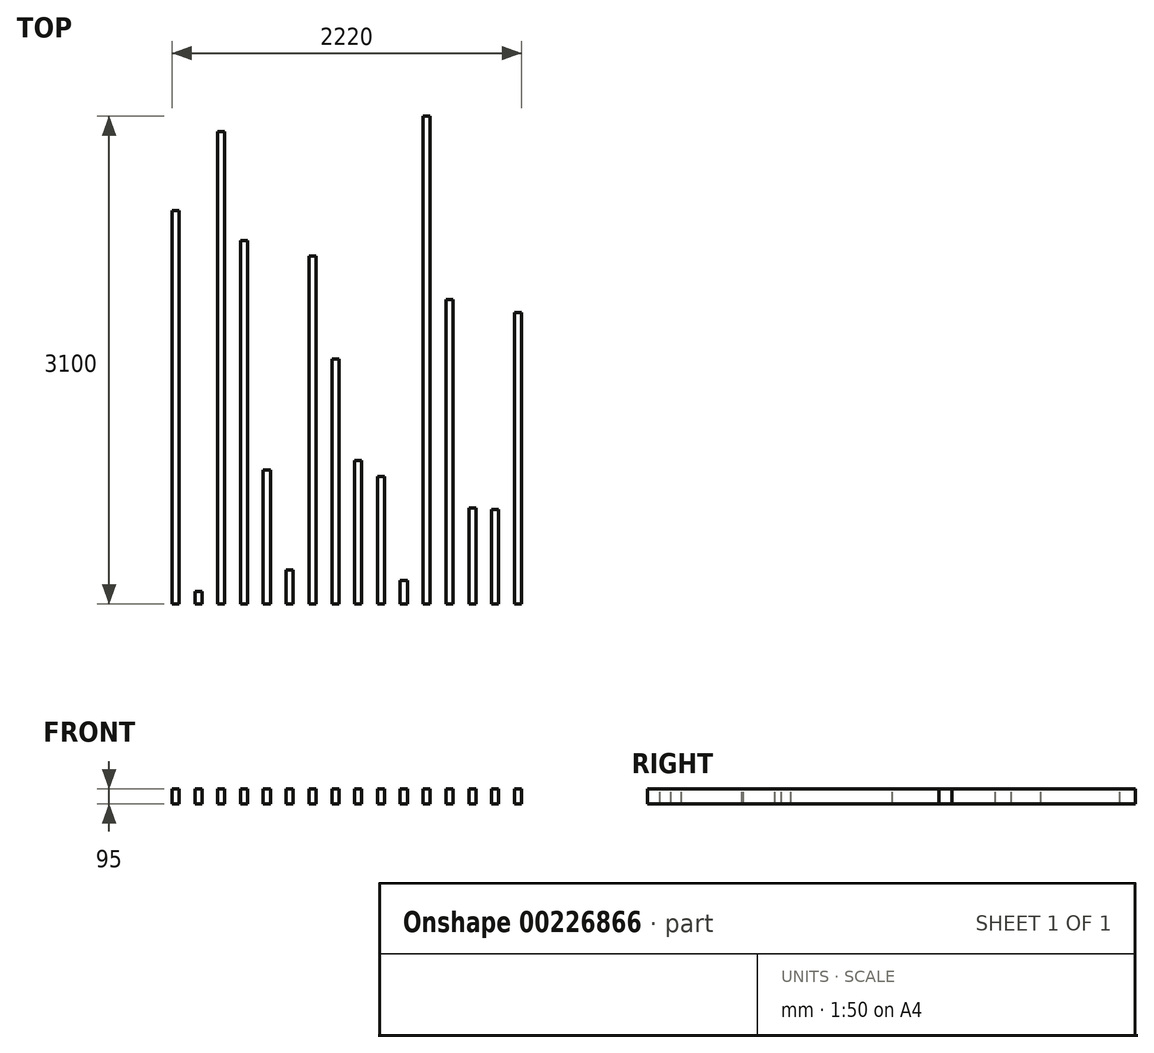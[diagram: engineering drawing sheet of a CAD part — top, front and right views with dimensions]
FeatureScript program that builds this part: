
annotation { "Feature Type Name" : "Feature", "Feature Type Description" : "" }
export const myFeature = defineFeature(function(context is Context, id is Id, definition is map)
    precondition{}
    {
        {
            var Q0;
            Q0=qCreatedBy(makeId("Front.planeOp"),FACE);
            var sketch = newSketch(context, id + "F0", { "sketchPlane" : qUnion([Q0])});
            skLineSegment(sketch, "E0.bottom", {"start": v(0, 0) * mm, "end": v(45, 0) * mm});
            skLineSegment(sketch, "E0.top", {"start": v(0, 95) * mm, "end": v(45, 95) * mm});
            skLineSegment(sketch, "E0.left", {"start": v(0, 0) * mm, "end": v(0, 95) * mm});
            skLineSegment(sketch, "E0.right", {"start": v(45, 0) * mm, "end": v(45, 95) * mm});
            skLineSegment(sketch, "E1.bottom", {"start": v(145, 0) * mm, "end": v(190, 0) * mm});
            skLineSegment(sketch, "E1.top", {"start": v(145, 95) * mm, "end": v(190, 95) * mm});
            skLineSegment(sketch, "E1.left", {"start": v(145, 0) * mm, "end": v(145, 95) * mm});
            skLineSegment(sketch, "E1.right", {"start": v(190, 0) * mm, "end": v(190, 95) * mm});
            skLineSegment(sketch, "E2.bottom", {"start": v(290, 0) * mm, "end": v(335, 0) * mm});
            skLineSegment(sketch, "E2.top", {"start": v(290, 95) * mm, "end": v(335, 95) * mm});
            skLineSegment(sketch, "E2.left", {"start": v(290, 0) * mm, "end": v(290, 95) * mm});
            skLineSegment(sketch, "E2.right", {"start": v(335, 0) * mm, "end": v(335, 95) * mm});
            skLineSegment(sketch, "E3.bottom", {"start": v(435, 0) * mm, "end": v(480, 0) * mm});
            skLineSegment(sketch, "E3.top", {"start": v(435, 95) * mm, "end": v(480, 95) * mm});
            skLineSegment(sketch, "E3.left", {"start": v(435, 0) * mm, "end": v(435, 95) * mm});
            skLineSegment(sketch, "E3.right", {"start": v(480, 0) * mm, "end": v(480, 95) * mm});
            skLineSegment(sketch, "E4.bottom", {"start": v(580, 0) * mm, "end": v(625, 0) * mm});
            skLineSegment(sketch, "E4.top", {"start": v(580, 95) * mm, "end": v(625, 95) * mm});
            skLineSegment(sketch, "E4.left", {"start": v(580, 0) * mm, "end": v(580, 95) * mm});
            skLineSegment(sketch, "E4.right", {"start": v(625, 0) * mm, "end": v(625, 95) * mm});
            skLineSegment(sketch, "E5.bottom", {"start": v(725, 0) * mm, "end": v(770, 0) * mm});
            skLineSegment(sketch, "E5.top", {"start": v(725, 95) * mm, "end": v(770, 95) * mm});
            skLineSegment(sketch, "E5.left", {"start": v(725, 0) * mm, "end": v(725, 95) * mm});
            skLineSegment(sketch, "E5.right", {"start": v(770, 0) * mm, "end": v(770, 95) * mm});
            skLineSegment(sketch, "E6.bottom", {"start": v(870, 0) * mm, "end": v(915, 0) * mm});
            skLineSegment(sketch, "E6.top", {"start": v(870, 95) * mm, "end": v(915, 95) * mm});
            skLineSegment(sketch, "E6.left", {"start": v(870, 0) * mm, "end": v(870, 95) * mm});
            skLineSegment(sketch, "E6.right", {"start": v(915, 0) * mm, "end": v(915, 95) * mm});
            skLineSegment(sketch, "E7.bottom", {"start": v(1015, 0) * mm, "end": v(1060, 0) * mm});
            skLineSegment(sketch, "E7.top", {"start": v(1015, 95) * mm, "end": v(1060, 95) * mm});
            skLineSegment(sketch, "E7.left", {"start": v(1015, 0) * mm, "end": v(1015, 95) * mm});
            skLineSegment(sketch, "E7.right", {"start": v(1060, 0) * mm, "end": v(1060, 95) * mm});
            skLineSegment(sketch, "E8.bottom", {"start": v(1160, 0) * mm, "end": v(1205, 0) * mm});
            skLineSegment(sketch, "E8.top", {"start": v(1160, 95) * mm, "end": v(1205, 95) * mm});
            skLineSegment(sketch, "E8.left", {"start": v(1160, 0) * mm, "end": v(1160, 95) * mm});
            skLineSegment(sketch, "E8.right", {"start": v(1205, 0) * mm, "end": v(1205, 95) * mm});
            skLineSegment(sketch, "E9.bottom", {"start": v(1305, 0) * mm, "end": v(1350, 0) * mm});
            skLineSegment(sketch, "E9.top", {"start": v(1305, 95) * mm, "end": v(1350, 95) * mm});
            skLineSegment(sketch, "E9.left", {"start": v(1305, 0) * mm, "end": v(1305, 95) * mm});
            skLineSegment(sketch, "E9.right", {"start": v(1350, 0) * mm, "end": v(1350, 95) * mm});
            skLineSegment(sketch, "E10.bottom", {"start": v(1450, 0) * mm, "end": v(1495, 0) * mm});
            skLineSegment(sketch, "E10.top", {"start": v(1450, 95) * mm, "end": v(1495, 95) * mm});
            skLineSegment(sketch, "E10.left", {"start": v(1450, 0) * mm, "end": v(1450, 95) * mm});
            skLineSegment(sketch, "E10.right", {"start": v(1495, 0) * mm, "end": v(1495, 95) * mm});
            skLineSegment(sketch, "E11.bottom", {"start": v(1595, 0) * mm, "end": v(1640, 0) * mm});
            skLineSegment(sketch, "E11.top", {"start": v(1595, 95) * mm, "end": v(1640, 95) * mm});
            skLineSegment(sketch, "E11.left", {"start": v(1595, 0) * mm, "end": v(1595, 95) * mm});
            skLineSegment(sketch, "E11.right", {"start": v(1640, 0) * mm, "end": v(1640, 95) * mm});
            skLineSegment(sketch, "E12.bottom", {"start": v(1740, 0) * mm, "end": v(1785, 0) * mm});
            skLineSegment(sketch, "E12.top", {"start": v(1740, 95) * mm, "end": v(1785, 95) * mm});
            skLineSegment(sketch, "E12.left", {"start": v(1740, 0) * mm, "end": v(1740, 95) * mm});
            skLineSegment(sketch, "E12.right", {"start": v(1785, 0) * mm, "end": v(1785, 95) * mm});
            skLineSegment(sketch, "E13.bottom", {"start": v(1885, 0) * mm, "end": v(1930, 0) * mm});
            skLineSegment(sketch, "E13.top", {"start": v(1885, 95) * mm, "end": v(1930, 95) * mm});
            skLineSegment(sketch, "E13.left", {"start": v(1885, 0) * mm, "end": v(1885, 95) * mm});
            skLineSegment(sketch, "E13.right", {"start": v(1930, 0) * mm, "end": v(1930, 95) * mm});
            skLineSegment(sketch, "E14.bottom", {"start": v(-100, 0) * mm, "end": v(-145, 0) * mm});
            skLineSegment(sketch, "E14.top", {"start": v(-100, 95) * mm, "end": v(-145, 95) * mm});
            skLineSegment(sketch, "E14.left", {"start": v(-100, 0) * mm, "end": v(-100, 95) * mm});
            skLineSegment(sketch, "E14.right", {"start": v(-145, 0) * mm, "end": v(-145, 95) * mm});
            skLineSegment(sketch, "E15.bottom", {"start": v(-245, 0) * mm, "end": v(-290, 0) * mm});
            skLineSegment(sketch, "E15.top", {"start": v(-245, 95) * mm, "end": v(-290, 95) * mm});
            skLineSegment(sketch, "E15.left", {"start": v(-245, 0) * mm, "end": v(-245, 95) * mm});
            skLineSegment(sketch, "E15.right", {"start": v(-290, 0) * mm, "end": v(-290, 95) * mm});
            skSolve(sketch);
        }
        {
            var Q0;
            Q0=makeQuery(id+"F0.imprint","IMPRINT",FACE,{"disambiguationData":[TD([[makeQuery(id+"F0.imprint","IMPRINT",EDGE,{"derivedFrom":sQuery(id+"F0.wireOp",EDGE,"E0.bottom")}),1.0]])]});
            extrude(context, id + "F1", {"entities" : qUnion([Q0]), "oppositeDirection" : true, "depth" : 3000 * mm});
        }
        {
            var Q0;
            Q0=makeQuery(id+"F0.imprint","IMPRINT",FACE,{"disambiguationData":[TD([[makeQuery(id+"F0.imprint","IMPRINT",EDGE,{"derivedFrom":sQuery(id+"F0.wireOp",EDGE,"E1.bottom")}),1.0]])]});
            extrude(context, id + "F2", {"entities" : qUnion([Q0]), "oppositeDirection" : true, "depth" : 2310 * mm});
        }
        {
            var Q0;
            Q0=makeQuery(id+"F0.imprint","IMPRINT",FACE,{"disambiguationData":[TD([[makeQuery(id+"F0.imprint","IMPRINT",EDGE,{"derivedFrom":sQuery(id+"F0.wireOp",EDGE,"E2.bottom")}),1.0]])]});
            extrude(context, id + "F3", {"entities" : qUnion([Q0]), "oppositeDirection" : true, "depth" : 850 * mm});
        }
        {
            var Q0;
            Q0=makeQuery(id+"F0.imprint","IMPRINT",FACE,{"disambiguationData":[TD([[makeQuery(id+"F0.imprint","IMPRINT",EDGE,{"derivedFrom":sQuery(id+"F0.wireOp",EDGE,"E3.bottom")}),1.0]])]});
            extrude(context, id + "F4", {"entities" : qUnion([Q0]), "oppositeDirection" : true, "depth" : 215 * mm});
        }
        {
            var Q0;
            Q0=makeQuery(id+"F0.imprint","IMPRINT",FACE,{"disambiguationData":[TD([[makeQuery(id+"F0.imprint","IMPRINT",EDGE,{"derivedFrom":sQuery(id+"F0.wireOp",EDGE,"E4.bottom")}),1.0]])]});
            extrude(context, id + "F5", {"entities" : qUnion([Q0]), "oppositeDirection" : true, "depth" : 2210 * mm});
        }
        {
            var Q0;
            Q0=makeQuery(id+"F0.imprint","IMPRINT",FACE,{"disambiguationData":[TD([[makeQuery(id+"F0.imprint","IMPRINT",EDGE,{"derivedFrom":sQuery(id+"F0.wireOp",EDGE,"E5.bottom")}),1.0]])]});
            extrude(context, id + "F6", {"entities" : qUnion([Q0]), "oppositeDirection" : true, "depth" : 1555 * mm});
        }
        {
            var Q0;
            Q0=makeQuery(id+"F0.imprint","IMPRINT",FACE,{"disambiguationData":[TD([[makeQuery(id+"F0.imprint","IMPRINT",EDGE,{"derivedFrom":sQuery(id+"F0.wireOp",EDGE,"E6.bottom")}),1.0]])]});
            extrude(context, id + "F7", {"entities" : qUnion([Q0]), "oppositeDirection" : true, "depth" : 910 * mm});
        }
        {
            var Q0;
            Q0=makeQuery(id+"F0.imprint","IMPRINT",FACE,{"disambiguationData":[TD([[makeQuery(id+"F0.imprint","IMPRINT",EDGE,{"derivedFrom":sQuery(id+"F0.wireOp",EDGE,"E7.bottom")}),1.0]])]});
            extrude(context, id + "F8", {"entities" : qUnion([Q0]), "oppositeDirection" : true, "depth" : 810 * mm});
        }
        {
            var Q0;
            Q0=makeQuery(id+"F0.imprint","IMPRINT",FACE,{"disambiguationData":[TD([[makeQuery(id+"F0.imprint","IMPRINT",EDGE,{"derivedFrom":sQuery(id+"F0.wireOp",EDGE,"E8.bottom")}),1.0]])]});
            extrude(context, id + "F9", {"entities" : qUnion([Q0]), "oppositeDirection" : true, "depth" : 150 * mm});
        }
        {
            var Q0;
            Q0=makeQuery(id+"F0.imprint","IMPRINT",FACE,{"disambiguationData":[TD([[makeQuery(id+"F0.imprint","IMPRINT",EDGE,{"derivedFrom":sQuery(id+"F0.wireOp",EDGE,"E9.bottom")}),1.0]])]});
            extrude(context, id + "F10", {"entities" : qUnion([Q0]), "oppositeDirection" : true, "depth" : 3100 * mm});
        }
        {
            var Q0;
            Q0=makeQuery(id+"F0.imprint","IMPRINT",FACE,{"disambiguationData":[TD([[makeQuery(id+"F0.imprint","IMPRINT",EDGE,{"derivedFrom":sQuery(id+"F0.wireOp",EDGE,"E10.bottom")}),1.0]])]});
            extrude(context, id + "F11", {"entities" : qUnion([Q0]), "oppositeDirection" : true, "depth" : 1935 * mm});
        }
        {
            var Q0;
            Q0=makeQuery(id+"F0.imprint","IMPRINT",FACE,{"disambiguationData":[TD([[makeQuery(id+"F0.imprint","IMPRINT",EDGE,{"derivedFrom":sQuery(id+"F0.wireOp",EDGE,"E11.bottom")}),1.0]])]});
            extrude(context, id + "F12", {"entities" : qUnion([Q0]), "oppositeDirection" : true, "depth" : 610 * mm});
        }
        {
            var Q0;
            Q0=makeQuery(id+"F0.imprint","IMPRINT",FACE,{"disambiguationData":[TD([[makeQuery(id+"F0.imprint","IMPRINT",EDGE,{"derivedFrom":sQuery(id+"F0.wireOp",EDGE,"E12.bottom")}),1.0]])]});
            extrude(context, id + "F13", {"entities" : qUnion([Q0]), "oppositeDirection" : true, "depth" : 600 * mm});
        }
        {
            var Q0;
            Q0=makeQuery(id+"F0.imprint","IMPRINT",FACE,{"disambiguationData":[TD([[makeQuery(id+"F0.imprint","IMPRINT",EDGE,{"derivedFrom":sQuery(id+"F0.wireOp",EDGE,"E13.bottom")}),1.0]])]});
            extrude(context, id + "F14", {"entities" : qUnion([Q0]), "oppositeDirection" : true, "depth" : 1850 * mm});
        }
        {
            var Q0;
            Q0=makeQuery(id+"F0.imprint","IMPRINT",FACE,{"disambiguationData":[TD([[makeQuery(id+"F0.imprint","IMPRINT",EDGE,{"derivedFrom":sQuery(id+"F0.wireOp",EDGE,"E14.bottom")}),-1.0]])]});
            extrude(context, id + "F15", {"entities" : qUnion([Q0]), "oppositeDirection" : true, "depth" : 80 * mm});
        }
        {
            var Q0;
            Q0=makeQuery(id+"F0.imprint","IMPRINT",FACE,{"disambiguationData":[TD([[makeQuery(id+"F0.imprint","IMPRINT",EDGE,{"derivedFrom":sQuery(id+"F0.wireOp",EDGE,"E15.bottom")}),-1.0]])]});
            extrude(context, id + "F16", {"entities" : qUnion([Q0]), "oppositeDirection" : true, "depth" : 2500 * mm});
        }
    });
